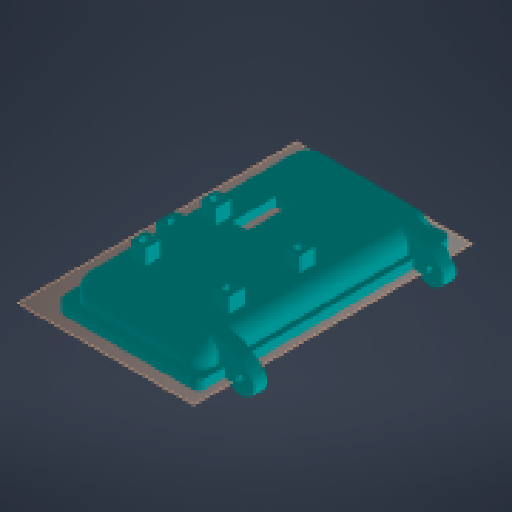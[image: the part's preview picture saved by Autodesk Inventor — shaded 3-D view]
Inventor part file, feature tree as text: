
AUTODESK INVENTOR PART (.ipt)
format: ipt  version: 2024 (Build 280153000, 153)  size: 477,184 bytes
history: native  units: mm
features: reference x32, other x15, extrude x8, sketch x8, projected_geometry x2, chamfer x1, fillet x1, shell x1, mirror x1
ambient origin geometry x8: Origin, YZ Plane, XZ Plane, XY Plane, X Axis, Y Axis, Z Axis, Center Point
bodies: Body1 (feature_tree)
feature tree (69):
  other  "Твердое тело1"
  extrude  "Выдавливание1"  Depth=2.0mm
  chamfer  "Фаска1"  Distance=3.0mm
  extrude  "Выдавливание2"  Depth=2.0mm TaperAngle=45.0deg
  other  "РабПлоскость1"
  other  "РабПлоскость2"
  extrude  "Выдавливание4"  Depth=15.5mm TaperAngle=0.0deg
  fillet  "Сопряжение1"  Radius=8.0mm
  extrude  "Выдавливание6"  Depth=45.0mm
  shell  "Оболочка1"  Thickness=95.0mm
  other  "Непосредственное редактирование2"
  other  "Непосредственное редактирование3"
  other  "РабПлоскость3"
  other  "РабПлоскость4"
  extrude  "Выдавливание10"  Depth=11.25mm TaperAngle=0.0deg
  extrude  "Выдавливание11"  Depth=8.0mm
  other  "РабПлоскость5"
  extrude  "Выдавливание13"  Depth=16.0mm TaperAngle=0.0deg
  mirror  "Зеркальное отражение5"
  other  "РабПлоскость6"
  extrude  "Выдавливание14"  Depth=4.0mm
  sketch  "Эскиз1"
  reference  "Ссылка1"
  reference  "Ссылка3"
  reference  "Ссылка4"
  reference  "Ссылка5"
  reference  "Ссылка6"
  reference  "Ссылка7"
  reference  "Ссылка8"
  reference  "Ссылка9"
  reference  "Ссылка10"
  sketch  "Эскиз2"
  reference  "Ссылка11"
  reference  "Ссылка12"
  reference  "Ссылка13"
  reference  "Ссылка14"
  reference  "Ссылка15"
  reference  "Ссылка16"
  reference  "Ссылка17"
  reference  "Ссылка18"
  reference  "Ссылка19"
  reference  "Ссылка20"
  reference  "Ссылка21"
  reference  "Ссылка22"
  sketch  "Эскиз4"
  projected_geometry  "Спроецированная петля1"
  sketch  "Эскиз6"
  projected_geometry  "Спроецированная петля2"
  sketch  "Эскиз11"
  sketch  "Эскиз12"
  reference  "Ссылка33"
  reference  "Ссылка34"
  sketch  "Эскиз14"
  reference  "Ссылка39"
  sketch  "Эскиз15"
  reference  "Ссылка40"
  reference  "Ссылка41"
  reference  "Ссылка42"
  reference  "Ссылка43"
  reference  "Ссылка44"
  reference  "Ссылка45"
  reference  "Ссылка46"
  reference  "Ссылка47"
  parser-record x1  (decoder bookkeeping rows leaked as tree rows — omitted from the tree; the rows remain in map.json)
  other  "front_box_asembly.iam"
  other  "front_box:1"
  other  "Перенос3"
  other  "Перенос4"
  other  "ts832:1"
note: 1 file-system path scrubbed to <path> (originals preserved in map.json)
